# Revit family: 0043506
name_source: partatom
category: Lighting Fixtures
revit_build: Autodesk Revit 2017 (Build: 20190507_1515(x64)
units: mm (PartAtom-declared; Revit-internal decimal feet)

## family parameters
Cut with Voids When Loaded = No
Host = Face
Light Source = Yes
OmniClass Number = 23.80.70.00
OmniClass Title = Lighting
Part Type = Normal
Room Calculation Point = No
Round Connector Dimension = Use Diameter
Shared = No

## types (16) — shared parameters
Apparent Load = 0 VA
Assembly Code = D5020200
AssetType = Fixed
ClassificationName = Uniclass2015
ClassificationValue = EF_70_80
Color Filter = 16777215
Default Elevation = 1219 mm
Dimming Lamp Color Temperature Shift = <None>
DocumentationLiterature = http://www.sylvania-lighting.com
Emit Shape Visible in Rendering = No
Emit from Circle Diameter = 610 mm
IfcExportAs = IfcLightFixtureType
IfcExportType = IfcLightFixtureType
Keynote = 16500
Lamp = LED
LampsType = LED
Manufacturer = Feilo Sylvania
ManufacturerName = Feilo Sylvania
Material_1_SYL = <By Category>
Material_2_SYL = <By Category>
Material_3_SYL = <By Category>
Material_4_SYL = <By Category>
SENSOR_SYL = 12 mm  [stored 0.0393701 ft]
Tilt Angle = -90.00°
Type Image = <None>
URL = http://www.sylvania-lighting.com
Voltage = 0 V
YIN_SENSOR_SYL = No
zero-valued in all types: Cost, NominalDepth, NominalHeight, NominalLength, PowerFactor

## per-type parameters (varying)
| type | BOTTOM_HEIGHT_SYL | BOTTOM_R_SYL | LUM_H_SYL | LUM_R_HEIGHT_SYL | LUM_R_SYL | Model | ModelNumber | ModelReference | Name | Photometric Web File | TypeName | Weight | YIN_180_SYL | YIN_250_SYL | YIN_330_SYL | YIN_360_SYL |
| 0043507_3000K SYLCIRCLE IP44 2050LM MW 830/840 DT | 85 mm  [stored 0.278871 ft] | 150 mm | 100 mm  [stored 0.328084 ft] | 70 mm | 180 mm  [stored 0.590551 ft] | SylCircle IP44 2050LM MW 830/840 DualTone | 0043507 | SylCircle IP44 2050LM MW 830/840 DualTone | SylCircle IP44 2050LM MW 830/840 DualTone | 0043507_3000K.ies | SylCircle IP44 2050LM MW 830/840 DualTone | 3.42 kg | No | No | No | Yes |
| 0043506_4000K SYLCIRCLE IP44 1550LM MW 830/840 DT | 81 mm  [stored 0.265748 ft] | 150 mm | 96 mm  [stored 0.314961 ft] | 66 mm  [stored 0.216535 ft] | 165 mm | SylCircle IP44 1550LM MW 830/840 DualTone | 0043506 | SylCircle IP44 1550LM MW 830/840 DualTone | SylCircle IP44 1550LM MW 830/840 DualTone | 0043506_4000K.ies | SylCircle IP44 1550LM MW 830/840 DualTone | 3.42 kg | No | No | Yes | No |
| 0043506_3000K SYLCIRCLE IP44 1550LM MW 830/840 DT | 81 mm  [stored 0.265748 ft] | 150 mm | 96 mm  [stored 0.314961 ft] | 66 mm  [stored 0.216535 ft] | 165 mm | SylCircle IP44 1550LM MW 830/840 DualTone | 0043506 | SylCircle IP44 1550LM MW 830/840 DualTone | SylCircle IP44 1550LM MW 830/840 DualTone | 0043506_3000K.ies | SylCircle IP44 1550LM MW 830/840 DualTone | 3.42 kg | No | No | Yes | No |
| 0043505_4000K SYLCIRCLE IP44 2050LM DIM 830/840 DT | 85 mm  [stored 0.278871 ft] | 150 mm | 100 mm  [stored 0.328084 ft] | 70 mm | 180 mm  [stored 0.590551 ft] | SylCircle IP44 2050LM DIM 830/840 DualTone | 0043505 | SylCircle IP44 2050LM DIM 830/840 DualTone | SylCircle IP44 2050LM DIM 830/840 DualTone | 0043505_4000K.ies | SylCircle IP44 2050LM DIM 830/840 DualTone | 3.54 kg | No | No | No | Yes |
| 0043505_3000K SYLCIRCLE IP44 2050LM DIM 830/840 DT | 85 mm  [stored 0.278871 ft] | 150 mm | 100 mm  [stored 0.328084 ft] | 70 mm | 180 mm  [stored 0.590551 ft] | SylCircle IP44 2050LM DIM 830/840 DualTone | 0043505 | SylCircle IP44 2050LM DIM 830/840 DualTone | SylCircle IP44 2050LM DIM 830/840 DualTone | 0043505_3000K.ies | SylCircle IP44 2050LM DIM 830/840 DualTone | 3.54 kg | No | No | No | Yes |
| 0043504_4000K SYLCIRCLE IP44 1550LM DIM 830/840 DT | 81 mm  [stored 0.265748 ft] | 150 mm | 96 mm  [stored 0.314961 ft] | 66 mm  [stored 0.216535 ft] | 165 mm | SylCircle IP44 1550LM DIM 830/840 DualTone | 0043504 | SylCircle IP44 1550LM DIM 830/840 DualTone | SylCircle IP44 1550LM DIM 830/840 DualTone | 0043504_4000K.ies | SylCircle IP44 1550LM DIM 830/840 DualTone | 3.54 kg | No | No | Yes | No |
| 0043504_3000K SYLCIRCLE IP44 1550LM DIM 830/840 DT | 81 mm  [stored 0.265748 ft] | 150 mm | 96 mm  [stored 0.314961 ft] | 66 mm  [stored 0.216535 ft] | 165 mm | SylCircle IP44 1550LM DIM 830/840 DualTone | 0043504 | SylCircle IP44 1550LM DIM 830/840 DualTone | SylCircle IP44 1550LM DIM 830/840 DualTone | 0043504_3000K.ies | SylCircle IP44 1550LM DIM 830/840 DualTone | 3.54 kg | No | No | Yes | No |
| 0043499_4000K SYLCIRCLE IP44 2050LM 830/840 DT | 85 mm  [stored 0.278871 ft] | 150 mm | 100 mm  [stored 0.328084 ft] | 70 mm | 180 mm  [stored 0.590551 ft] | SylCircle IP44 2050lm 830/840 DualTone | 0043499 | SylCircle IP44 2050lm 830/840 DualTone | SylCircle IP44 2050lm 830/840 DualTone | 0043499_4000K.ies | SylCircle IP44 2050lm 830/840 DualTone | 3.12 kg | No | No | No | Yes |
| 0043499_3000K SYLCIRCLE IP44 2050LM 830/840 DT | 85 mm  [stored 0.278871 ft] | 150 mm | 100 mm  [stored 0.328084 ft] | 70 mm | 180 mm  [stored 0.590551 ft] | SylCircle IP44 2050lm 830/840 DualTone | 0043499 | SylCircle IP44 2050lm 830/840 DualTone | SylCircle IP44 2050lm 830/840 DualTone | 0043499_3000K.ies | SylCircle IP44 2050lm 830/840 DualTone | 3.12 kg | No | No | No | Yes |
| 0043498_4000K SYLCIRCLE IP44 1550LM 830/840 DT | 81 mm  [stored 0.265748 ft] | 150 mm | 96 mm  [stored 0.314961 ft] | 66 mm  [stored 0.216535 ft] | 165 mm | SylCircle IP44 1550lm 830/840 DualTone | 0043498 | SylCircle IP44 1550lm 830/840 DualTone | SylCircle IP44 1550lm 830/840 DualTone | 0043498_4000K.ies | SylCircle IP44 1550lm 830/840 DualTone | 3.12 kg | No | No | Yes | No |
| 0043498_3000K SYLCIRCLE IP44 1550LM 830/840 DT | 81 mm  [stored 0.265748 ft] | 150 mm | 96 mm  [stored 0.314961 ft] | 66 mm  [stored 0.216535 ft] | 165 mm | SylCircle IP44 1550lm 830/840 DualTone | 0043498 | SylCircle IP44 1550lm 830/840 DualTone | SylCircle IP44 1550lm 830/840 DualTone | 0043498_3000K.ies | SylCircle IP44 1550lm 830/840 DualTone | 3.12 kg | No | No | Yes | No |
| 0043497_4000K SYLCIRCLE IP44 1025LM 830/840 DT | 65 mm  [stored 0.213255 ft] | 110 mm  [stored 0.360892 ft] | 80 mm  [stored 0.262467 ft] | 50 mm  [stored 0.164042 ft] | 125 mm  [stored 0.410105 ft] | SylCircle IP44 1025lm 830/840 DualTone | 0043497 | SylCircle IP44 1025lm 830/840 DualTone | SylCircle IP44 1025lm 830/840 DualTone | 0043497_4000K.ies | SylCircle IP44 1025lm 830/840 DualTone | 1.5 kg | No | Yes | No | No |
| 0043497_3000K SYLCIRCLE IP44 1025LM 830/840 DT | 65 mm  [stored 0.213255 ft] | 110 mm  [stored 0.360892 ft] | 80 mm  [stored 0.262467 ft] | 50 mm  [stored 0.164042 ft] | 125 mm  [stored 0.410105 ft] | SylCircle IP44 1025lm 830/840 DualTone | 0043497 | SylCircle IP44 1025lm 830/840 DualTone | SylCircle IP44 1025lm 830/840 DualTone | 0043497_3000K.ies | SylCircle IP44 1025lm 830/840 DualTone | 1.5 kg | No | Yes | No | No |
| 0043496_4000K SYLCIRCLE IP44 520LM 830/840 DT | 60 mm | 76 mm  [stored 0.249344 ft] | 75 mm | 45 mm | 90 mm  [stored 0.295276 ft] | SylCircle IP44 520lm 830/840 DualTone | 0043496 | SylCircle IP44 520lm 830/840 DualTone | SylCircle IP44 520lm 830/840 DualTone | 0043496_4000K.ies | SylCircle IP44 520lm 830/840 DualTone | 1.02 kg | Yes | No | No | No |
| 0043496_3000K SYLCIRCLE IP44 520LM 830/840 DT | 60 mm | 76 mm  [stored 0.249344 ft] | 75 mm | 45 mm | 90 mm  [stored 0.295276 ft] | SylCircle IP44 520lm 830/840 DualTone | 0043496 | SylCircle IP44 520lm 830/840 DualTone | SylCircle IP44 520lm 830/840 DualTone | 0043496_3000K.ies | SylCircle IP44 520lm 830/840 DualTone | 1.02 kg | Yes | No | No | No |
| 0043507_4000K SYLCIRCLE IP44 2050LM MW 830/840 DT | 85 mm  [stored 0.278871 ft] | 150 mm | 100 mm  [stored 0.328084 ft] | 70 mm | 180 mm  [stored 0.590551 ft] | SylCircle IP44 2050LM MW 830/840 DualTone | 0043507 | SylCircle IP44 2050LM MW 830/840 DualTone | SylCircle IP44 2050LM MW 830/840 DualTone | 0043507_4000K.ies | SylCircle IP44 2050LM MW 830/840 DualTone | 3.42 kg | No | No | No | Yes |

note: [stored X ft] marks values corroborated as IEEE doubles in the binary element streams (Revit-internal decimal feet)

## geometry (parser evidence)
native form markers: Sweep x1
no freeform markers — native parametric forms only
